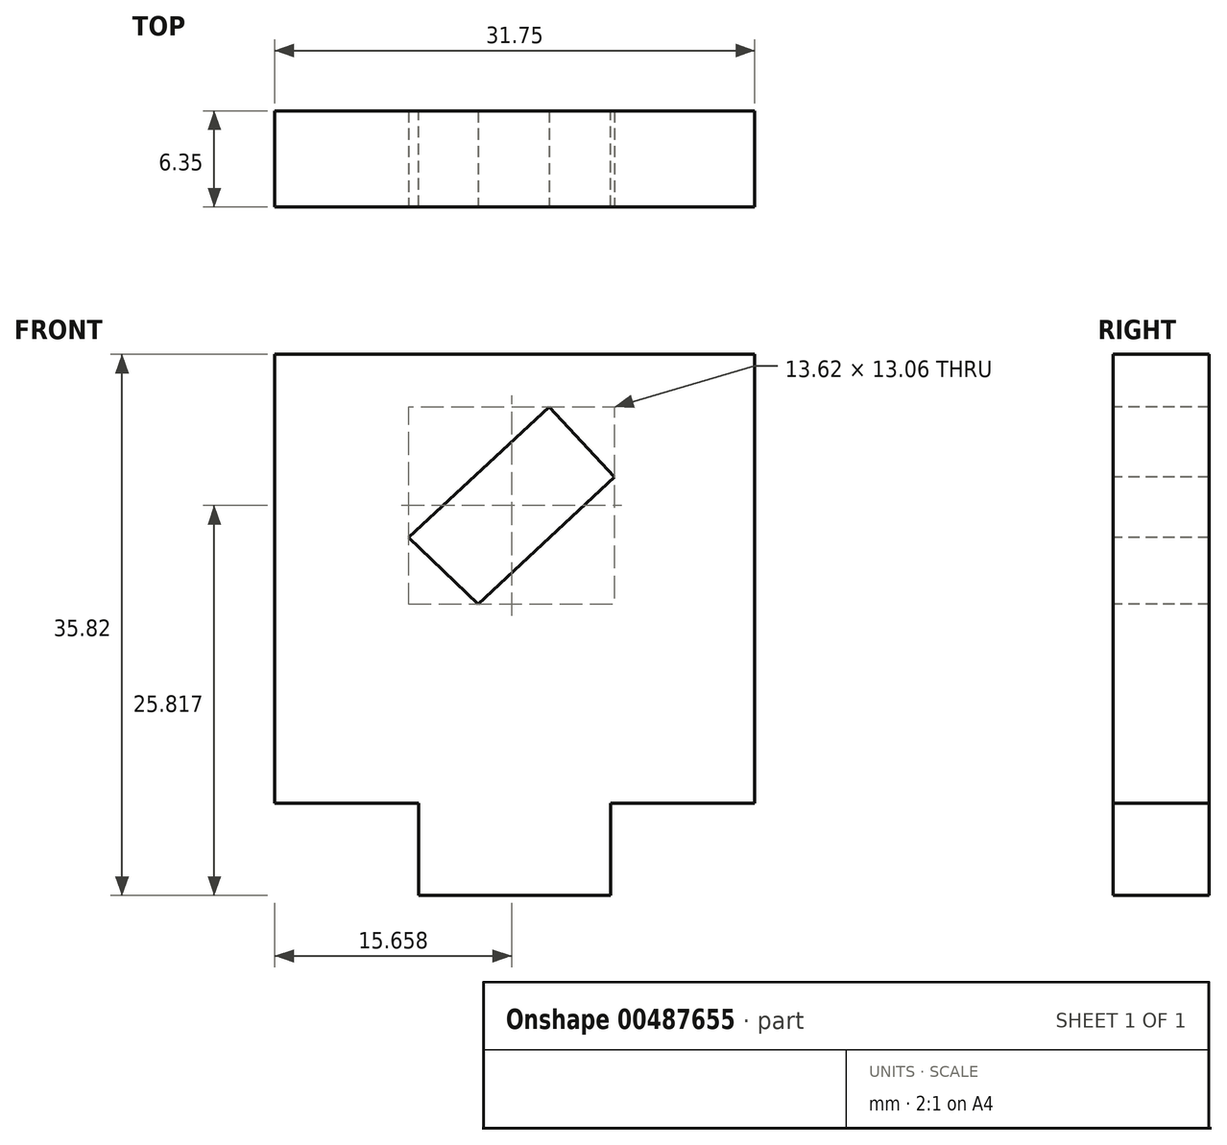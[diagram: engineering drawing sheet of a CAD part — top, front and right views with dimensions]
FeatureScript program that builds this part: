
annotation { "Feature Type Name" : "Feature", "Feature Type Description" : "" }
export const myFeature = defineFeature(function(context is Context, id is Id, definition is map)
    precondition{}
    {
        {
            var Q0;
            Q0=qCreatedBy(makeId("Front.planeOp"),FACE);
            var sketch = newSketch(context, id + "F0", { "sketchPlane" : qUnion([Q0])});
            skLineSegment(sketch, "E0.bottom", {"start": v(0, 0) * mm, "end": v(31.75, 0) * mm});
            skLineSegment(sketch, "E0.top", {"start": v(0, 29.72) * mm, "end": v(31.75, 29.72) * mm});
            skLineSegment(sketch, "E0.left", {"start": v(0, 0) * mm, "end": v(0, 29.72) * mm});
            skLineSegment(sketch, "E0.right", {"start": v(31.75, 0) * mm, "end": v(31.75, 29.72) * mm});
            skLineSegment(sketch, "E1.bottom", {"start": v(9.53, 0) * mm, "end": v(22.23, 0) * mm});
            skLineSegment(sketch, "E1.top", {"start": v(9.53, -6.1) * mm, "end": v(22.23, -6.1) * mm});
            skLineSegment(sketch, "E1.left", {"start": v(9.53, 0) * mm, "end": v(9.53, -6.1) * mm});
            skLineSegment(sketch, "E1.right", {"start": v(22.23, 0) * mm, "end": v(22.23, -6.1) * mm});
            skSolve(sketch);
        }
        {
            var Q0;
            {Q0=qUnion([makeQuery(id+"F0.imprint","IMPRINT",FACE,{"disambiguationData":[TD([[makeQuery(id+"F0.imprint","IMPRINT",EDGE,{"derivedFrom":sQuery(id+"F0.wireOp",EDGE,"E0.top")}),-1.0]])]}),makeQuery(id+"F0.imprint","IMPRINT",FACE,{"disambiguationData":[TD([[makeQuery(id+"F0.imprint","IMPRINT",EDGE,{"derivedFrom":sQuery(id+"F0.wireOp",EDGE,"E1.top")}),1.0]])]})]);}
            extrude(context, id + "F1", {"entities" : qUnion([Q0]), "depth" : 6.35 * mm});
        }
        {
            var Q0;
            Q0=makeQuery(id+"F1.opExtrude","CAP_FACE",FACE,{"disambiguationData":[OSD([sQuery(id+"F0.wireOp",EDGE,"E0.bottom"),sQuery(id+"F0.wireOp",EDGE,"E0.top"),sQuery(id+"F0.wireOp",EDGE,"E0.left"),sQuery(id+"F0.wireOp",EDGE,"E0.right"),sQuery(id+"F0.wireOp",EDGE,"E1.top"),sQuery(id+"F0.wireOp",EDGE,"E1.left"),sQuery(id+"F0.wireOp",EDGE,"E1.right")])],"isStart":false});
            var sketch = newSketch(context, id + "F2", { "sketchPlane" : qUnion([Q0])});
            skLineSegment(sketch, "E2", {"start": v(15.67, 29.72) * mm, "end": v(15.67, 8.81) * mm, "construction": true});
            skLineSegment(sketch, "E3", {"start": v(18.85, 19.57) * mm, "end": v(11.08, 19.57) * mm, "construction": true});
            skPoint(sketch, "E3.endSnap0", {"position": v(12.5, 19.57) * mm});
            skPoint(sketch, "E4.middle", {"position": v(15.67, 19.6) * mm});
            skLineSegment(sketch, "E5", {"start": v(15.67, 19.6) * mm, "end": v(24.1, 27.47) * mm, "construction": true});
            skLineSegment(sketch, "E6", {"start": v(18.14, 26.25) * mm, "end": v(8.85, 17.58) * mm});
            skLineSegment(sketch, "E7.MirrorCS", {"start": v(22.47, 21.6) * mm, "end": v(13.45, 13.19) * mm});
            skLineSegment(sketch, "E8", {"start": v(18.14, 26.25) * mm, "end": v(13.45, 13.19) * mm, "construction": true});
            skLineSegment(sketch, "E9", {"start": v(22.47, 21.6) * mm, "end": v(8.85, 17.58) * mm, "construction": true});
            skLineSegment(sketch, "E10", {"start": v(18.14, 26.25) * mm, "end": v(22.47, 21.6) * mm});
            skLineSegment(sketch, "E11", {"start": v(8.85, 17.58) * mm, "end": v(13.45, 13.19) * mm});
            skSolve(sketch);
        }
        {
            var Q0;
            Q0=qSketchRegion(id+"F2",true);
            extrude(context, id + "F3", {"entities" : qUnion([Q0]), "operationType" : NewBodyOperationType.REMOVE, "oppositeDirection" : true, "depth" : 25.4 * mm});
        }
    });
